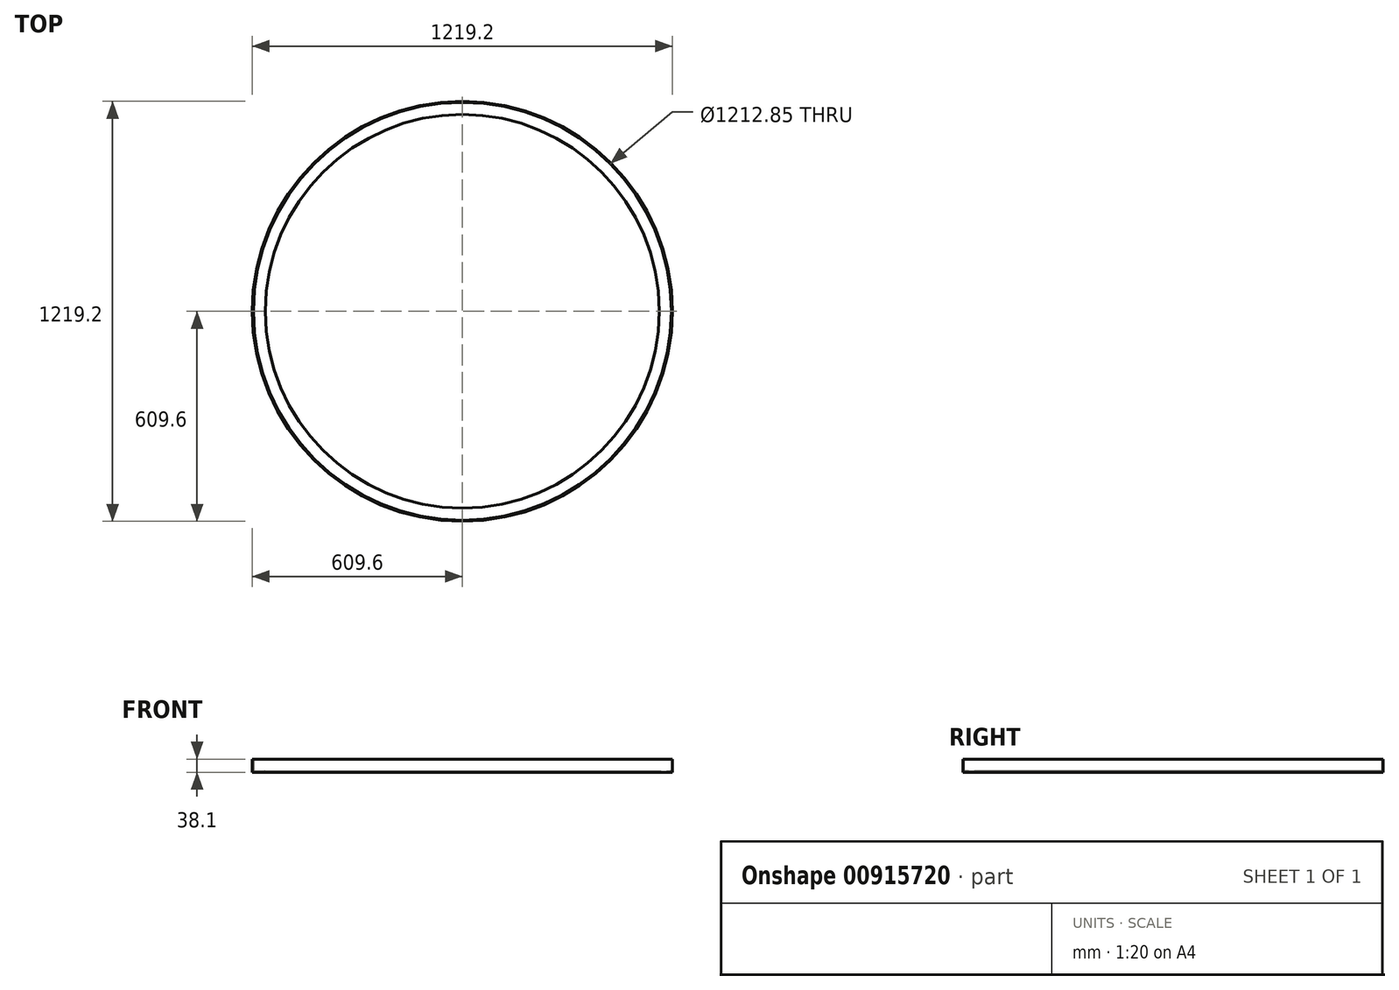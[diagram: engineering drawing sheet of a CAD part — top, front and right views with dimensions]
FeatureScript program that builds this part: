
annotation { "Feature Type Name" : "Feature", "Feature Type Description" : "" }
export const myFeature = defineFeature(function(context is Context, id is Id, definition is map)
    precondition{}
    {
        {
            var Q0;
            Q0=qCreatedBy(makeId("Front.planeOp"),FACE);
            var sketch = newSketch(context, id + "F0", { "sketchPlane" : qUnion([Q0])});
            skLineSegment(sketch, "E0", {"start": v(0, 38.1) * mm, "end": v(0, 0) * mm});
            skLineSegment(sketch, "E1", {"start": v(0, 0) * mm, "end": v(38.1, 0) * mm});
            skLineSegment(sketch, "E2", {"start": v(38.1, 0) * mm, "end": v(38.1, 0) * mm});
            skLineSegment(sketch, "E3", {"start": v(34.93, 3.18) * mm, "end": v(6.35, 3.17) * mm});
            skLineSegment(sketch, "E4", {"start": v(3.18, 6.35) * mm, "end": v(3.18, 34.93) * mm});
            skLineSegment(sketch, "E5", {"start": v(0, 38.1) * mm, "end": v(0, 38.1) * mm});
            skPoint(sketch, "E6.visualSharp", {"position": v(3.18, 3.17) * mm});
            skArc(sketch, "E6.filletArc", {"start": v(3.18, 6.35) * mm, "mid": v(4.1, 4.1) * mm, "end": v(6.35, 3.17) * mm});
            skPoint(sketch, "E7.visualSharp", {"position": v(3.18, 38.1) * mm});
            skArc(sketch, "E7.filletArc", {"start": v(3.17, 34.93) * mm, "mid": v(2.25, 37.17) * mm, "end": v(0, 38.1) * mm});
            skPoint(sketch, "E8.visualSharp", {"position": v(38.1, 3.18) * mm});
            skArc(sketch, "E8.filletArc", {"start": v(38.1, 0) * mm, "mid": v(37.17, 2.25) * mm, "end": v(34.93, 3.17) * mm});
            skSolve(sketch);
        }
        {
            var Q0;
            Q0=qCreatedBy(makeId("Top.planeOp"),FACE);
            var sketch = newSketch(context, id + "F1", { "sketchPlane" : qUnion([Q0])});
            skCircle(sketch, "E9", {"center": v(609.6, 0) * mm, "radius": 609.6 * mm});
            skPoint(sketch, "E9.first.point", {"position": v(0, 0) * mm});
            skPoint(sketch, "E9.second.point", {"position": v(1219.2, 0) * mm});
            skPoint(sketch, "E9.third.point", {"position": v(553.16, -606.98) * mm});
            skSolve(sketch);
        }
        {
            var Q0;
            Q0=makeQuery(id+"F0.imprint","IMPRINT",FACE,{"disambiguationData":[TD([[makeQuery(id+"F0.imprint","IMPRINT",EDGE,{"derivedFrom":sQuery(id+"F0.wireOp",EDGE,"E0")}),1.0]])]});
            var Q1;
            Q1=sQuery(id+"F1.wireOp",EDGE,"E9");
            revolve(context, id + "F2", {"surfaceOperationType" : NewSurfaceOperationType.NEW, "entities" : qUnion([Q0]), "axis" : qUnion([Q1]), "revolveType" : RevolveType.FULL});
        }
    });
